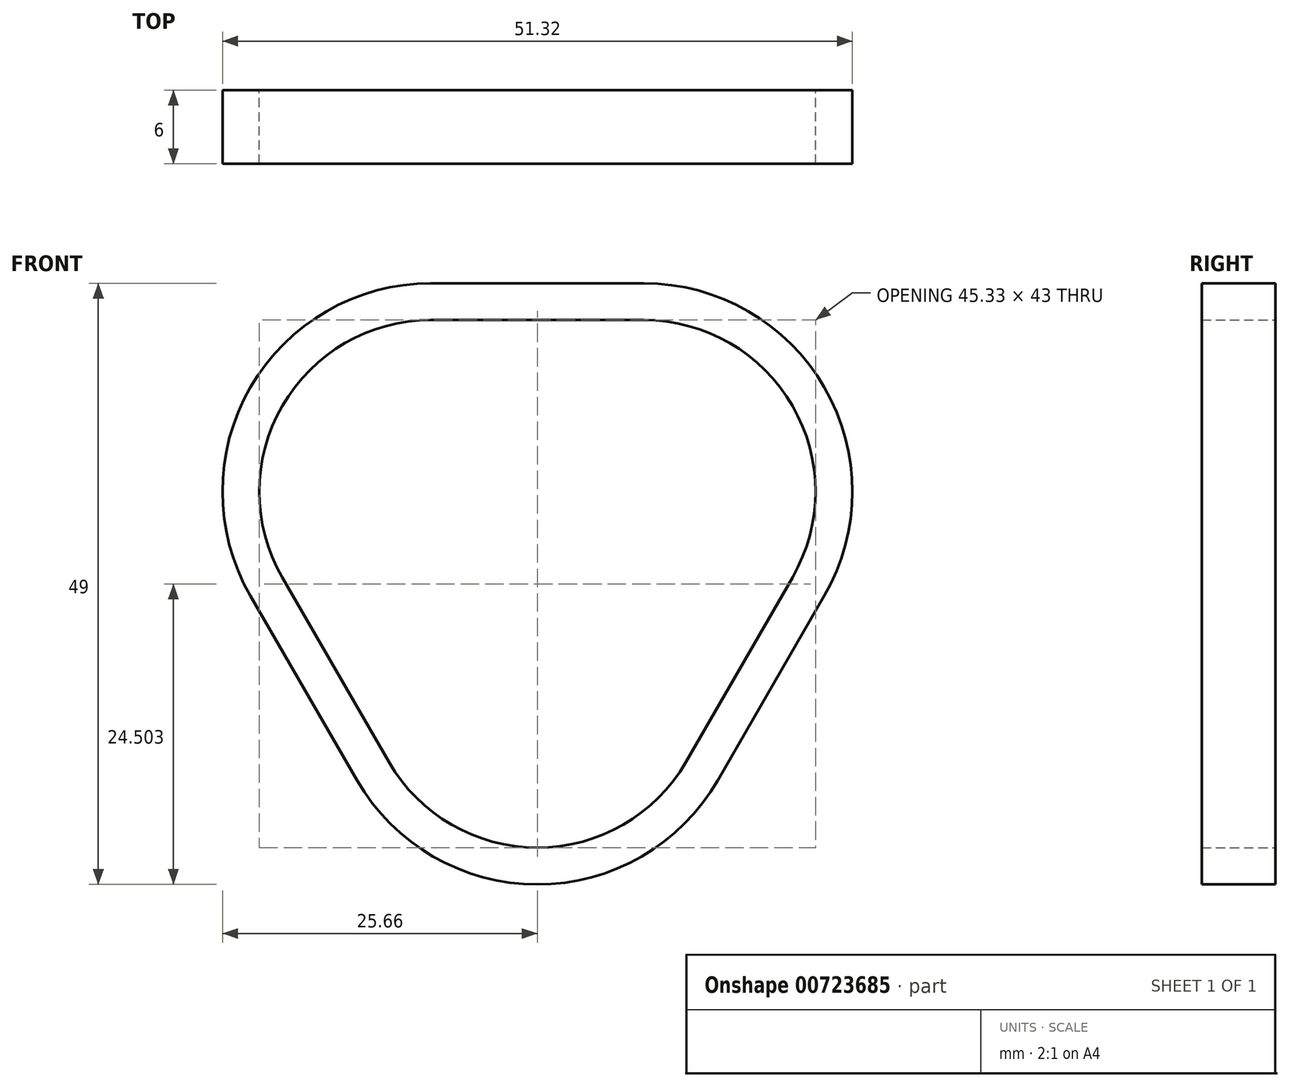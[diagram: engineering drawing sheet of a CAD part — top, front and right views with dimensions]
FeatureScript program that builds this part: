
annotation { "Feature Type Name" : "Feature", "Feature Type Description" : "" }
export const myFeature = defineFeature(function(context is Context, id is Id, definition is map)
    precondition{}
    {
        {
            var Q0;
            Q0=qCreatedBy(makeId("Front.planeOp"),FACE);
            var sketch = newSketch(context, id + "F0", { "sketchPlane" : qUnion([Q0])});
            skCircle(sketch, "E0.cCircle", {"center": v(0, 0) * mm, "radius": 19 * mm, "construction": true});
            skLineSegment(sketch, "E0.0", {"start": v(-8.68, 19) * mm, "end": v(8.68, 19) * mm});
            skLineSegment(sketch, "E0.1", {"start": v(20.8, -1.98) * mm, "end": v(12.1, -17.02) * mm});
            skLineSegment(sketch, "E0.2", {"start": v(-12.1, -17.02) * mm, "end": v(-20.8, -1.98) * mm});
            skPoint(sketch, "E0.0.midPoint", {"position": v(0, 19) * mm});
            skPoint(sketch, "E1.visualSharp", {"position": v(-32.9, 19) * mm});
            skArc(sketch, "E1.filletArc", {"start": v(-8.68, 19) * mm, "mid": v(-20.8, 12) * mm, "end": v(-20.8, -1.98) * mm});
            skPoint(sketch, "E2.visualSharp", {"position": v(32.9, 19) * mm});
            skArc(sketch, "E2.filletArc", {"start": v(20.8, -1.98) * mm, "mid": v(20.8, 12) * mm, "end": v(8.68, 19) * mm});
            skPoint(sketch, "E3.visualSharp", {"position": v(0, -37.99) * mm});
            skArc(sketch, "E3.filletArc", {"start": v(-12.1, -17.02) * mm, "mid": v(0, -24) * mm, "end": v(12.1, -17.02) * mm});
            skLineSegment(sketch, "E4.0", {"start": v(23.39, -3.48) * mm, "end": v(14.7, -18.52) * mm});
            skLineSegment(sketch, "E4.1", {"start": v(-8.68, 22) * mm, "end": v(8.68, 22) * mm});
            skArc(sketch, "E4.2", {"start": v(-8.68, 22) * mm, "mid": v(-23.39, 13.5) * mm, "end": v(-23.39, -3.48) * mm});
            skArc(sketch, "E4.3", {"start": v(23.39, -3.48) * mm, "mid": v(23.39, 13.5) * mm, "end": v(8.68, 22) * mm});
            skLineSegment(sketch, "E4.4", {"start": v(-14.7, -18.52) * mm, "end": v(-23.39, -3.48) * mm});
            skArc(sketch, "E4.5", {"start": v(-14.7, -18.52) * mm, "mid": v(0, -27) * mm, "end": v(14.7, -18.52) * mm});
            skSolve(sketch);
        }
        {
            var Q0;
            Q0=makeQuery(id+"F0.imprint","IMPRINT",FACE,{"disambiguationData":[TD([[makeQuery(id+"F0.imprint","IMPRINT",EDGE,{"derivedFrom":sQuery(id+"F0.wireOp",EDGE,"E0.0")}),1.0]])]});
            extrude(context, id + "F1", {"entities" : qUnion([Q0]), "depth" : 6 * mm, "offsetDistance" : 25 * mm});
        }
    });
